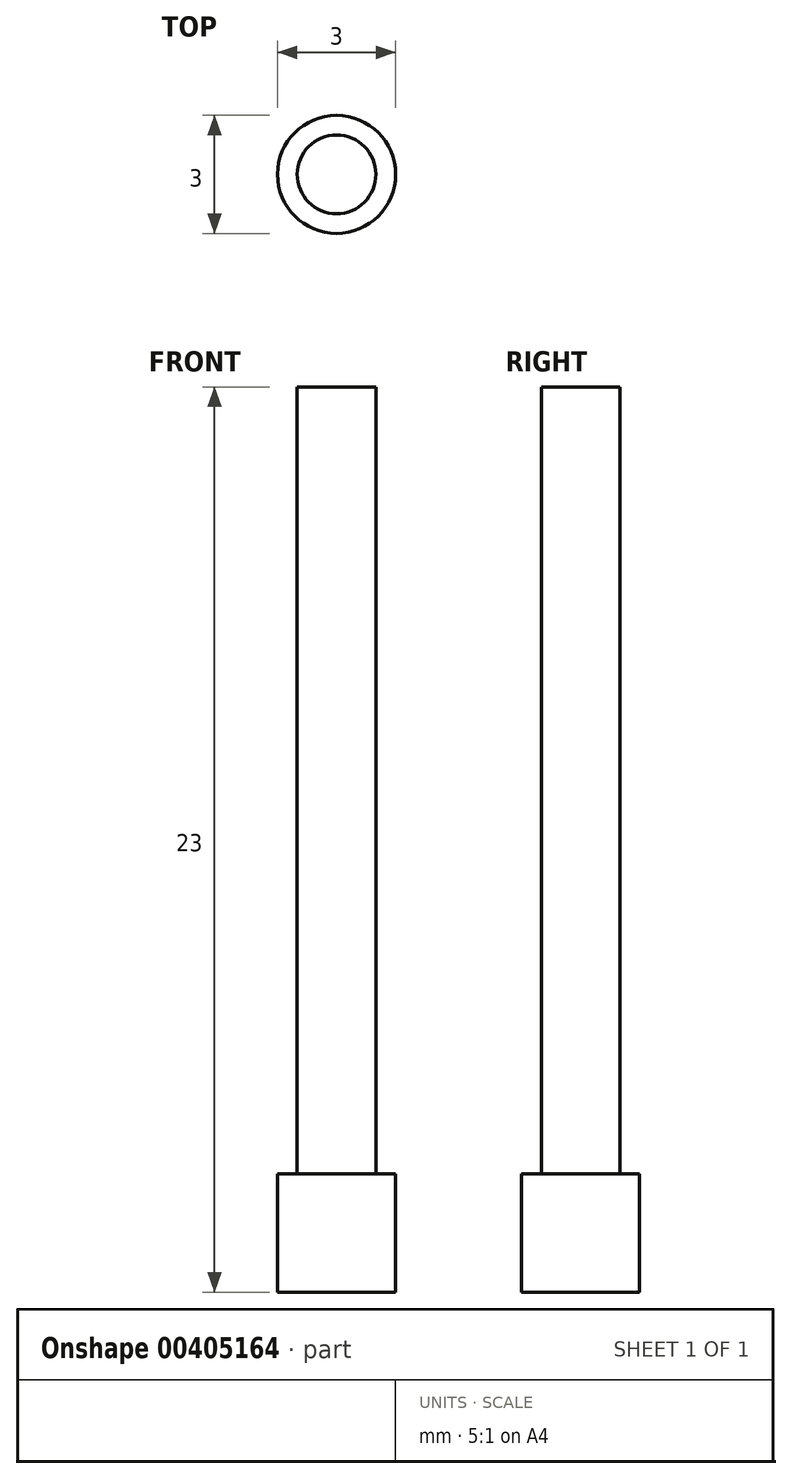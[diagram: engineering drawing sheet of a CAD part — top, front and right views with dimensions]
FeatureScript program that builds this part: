
annotation { "Feature Type Name" : "Feature", "Feature Type Description" : "" }
export const myFeature = defineFeature(function(context is Context, id is Id, definition is map)
    precondition{}
    {
        {
            var Q0;
            Q0=qCreatedBy(makeId("Top.planeOp"),FACE);
            var sketch = newSketch(context, id + "F0", { "sketchPlane" : qUnion([Q0])});
            skCircle(sketch, "E0", {"center": v(0, 0) * mm, "radius": 1.5 * mm});
            skSolve(sketch);
        }
        {
            var Q0;
            Q0=makeQuery(id+"F0.imprint","IMPRINT",FACE,{"disambiguationData":[TD([[makeQuery(id+"F0.imprint","IMPRINT",EDGE,{"derivedFrom":sQuery(id+"F0.wireOp",EDGE,"E0")}),1.0]])]});
            extrude(context, id + "F1", {"entities" : qUnion([Q0]), "depth" : 3 * mm, "hasDraft" : true, "draftAngle" : 0 * degree});
        }
        {
            var Q0;
            Q0=makeQuery(id+"F1.opExtrude","CAP_FACE",FACE,{"disambiguationData":[OSD([sQuery(id+"F0.wireOp",EDGE,"E0")])],"isStart":false});
            var sketch = newSketch(context, id + "F2", { "sketchPlane" : qUnion([Q0])});
            skCircle(sketch, "E1", {"center": v(0, 0) * mm, "radius": 1 * mm});
            skSolve(sketch);
        }
        {
            var Q0;
            Q0 = qSketchRegion(id + "F2", true);
            extrude(context, id + "F3", {"entities" : qUnion([Q0]), "operationType" : NewBodyOperationType.ADD, "depth" : 20 * mm});
        }
    });
